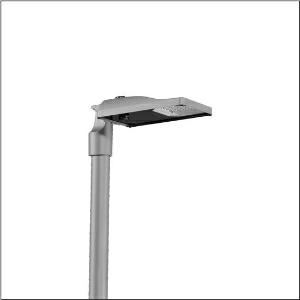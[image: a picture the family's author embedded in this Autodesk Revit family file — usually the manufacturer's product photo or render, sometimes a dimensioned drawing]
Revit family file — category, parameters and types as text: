
# Revit family: streetlight_sl_31_micro___pl52_5xh5h31t08da_3d46
name_source: partatom
category: Lighting Fixtures
units: mm (PartAtom-declared; Revit-internal decimal feet)

## family parameters
Cut with Voids When Loaded = No
Host = Face
Light Source = No
Part Type = Normal
Room Calculation Point = No
Round Connector Dimension = Use Diameter
Shared = No

## types (1)
- --- (1 x LED, 4850 lm, 37.7 W, 3000K)
    Apparent Load = 38 VA
    CIE Flux Codes = 27 59 98 100 100
    Color Rendering = 70
    Color Temperature = 3000K
    Default Elevation = 1800 mm
    Description = Streetlight SL 31 micro D4i, Desk-Remote mast luminaire for post-top, side-entry; light control with lens of PMMA; light distribution: PL52, direct asymmetric distribution, for standard-compliant lighting for roads and squares; LED: luminous flux: 4.850lm, light colour: 730, colour temperature: 3000K; luminous efficacy: 128,6lm/W; control: pre-setting: logarithmic dimming characteristic, flexible luminous flux parameterisation, time-dependent luminous flux control, constant luminous flux control, power reduction, intelligent temperature release in ECG and LED module, overheat protection; luminaire housing, of diecast aluminium, SITECO metallic grey (DB 702S), corrosivity category C5 high according to DIN EN ISO 12944; cover of toughened safety glass, transparent, opened without tools; mast flange of diecast aluminium, SITECO metallic grey (DB 702S), spigot size: 76/60mm, mast flange included unmounted; with cable H07RN-F 2x 1.5mm², cable length: 6,5m, connection cable pre-assembled; mains connection: 220..240V, AC, 50/60Hz; power consumption (at start of service life): 37,7W / (at end of service life): 40,9W / (with reduced operation 50%): 16,3W; protection rating (complete): IP66; insulation class (complete): insulation class II (safety insulation); impact resistance: IK09; certification: CE, ENEC, ENEC+, VDE, UKCA, ZD4i; permissible operating ambient temperature for outdoor applications: -40..+50°C; packaging unit: 1 piece

Light Distribution: PL52
    Height = 76 mm
    Lamp = 1 x LED
    Lamp Light Flux = 4850 lm
    Lamp Power = 37.7 W
    Lamp count = 1
    Length = 467 mm
    Luminous efficacy = 129 lm/W
    Manufacturer = Siteco
    ModVariant = No
    Model = 5XH5H31T08DA
    Mounting Place = Pole
    Mounting Type = Pole top
    Number of Poles = 1
    OnlyDefault = Yes
    Power Factor = 1
    Product Name = Streetlight SL 31 micro | PL52
    Product group = mast luminaire | pylon top
    ProductGroupID = 6100
    Protection Class = Protection class II
    Protection Degree = IP 66
    RLX_Detail_Level = 1
    RLX_Emergency_Light_Flux = 0 lm
    RLX_Emergency_Type = 0
    RLX_Emergency_Type_DB = No
    RlxData = <blob elided: 53829 chars, md5=8f33b0d9>
    Socket = socket
    Standby Power = 0 W
    System Light Flux = 4850 lm
    System Power = 38 W
    Type Comments = factory setting: luminous flux: 100 % | dim-lin: 254 | 745 mA
    Type Image = l_1300315.jpg
    URL = http://relux.com
    VarID = @adj_057065
    Voltage = 0 V
    Weight = 0.00 kg
    Width = 265 mm

## geometry (parser evidence)
native form markers: Blend x4, Sweep x12
no freeform markers — native parametric forms only
